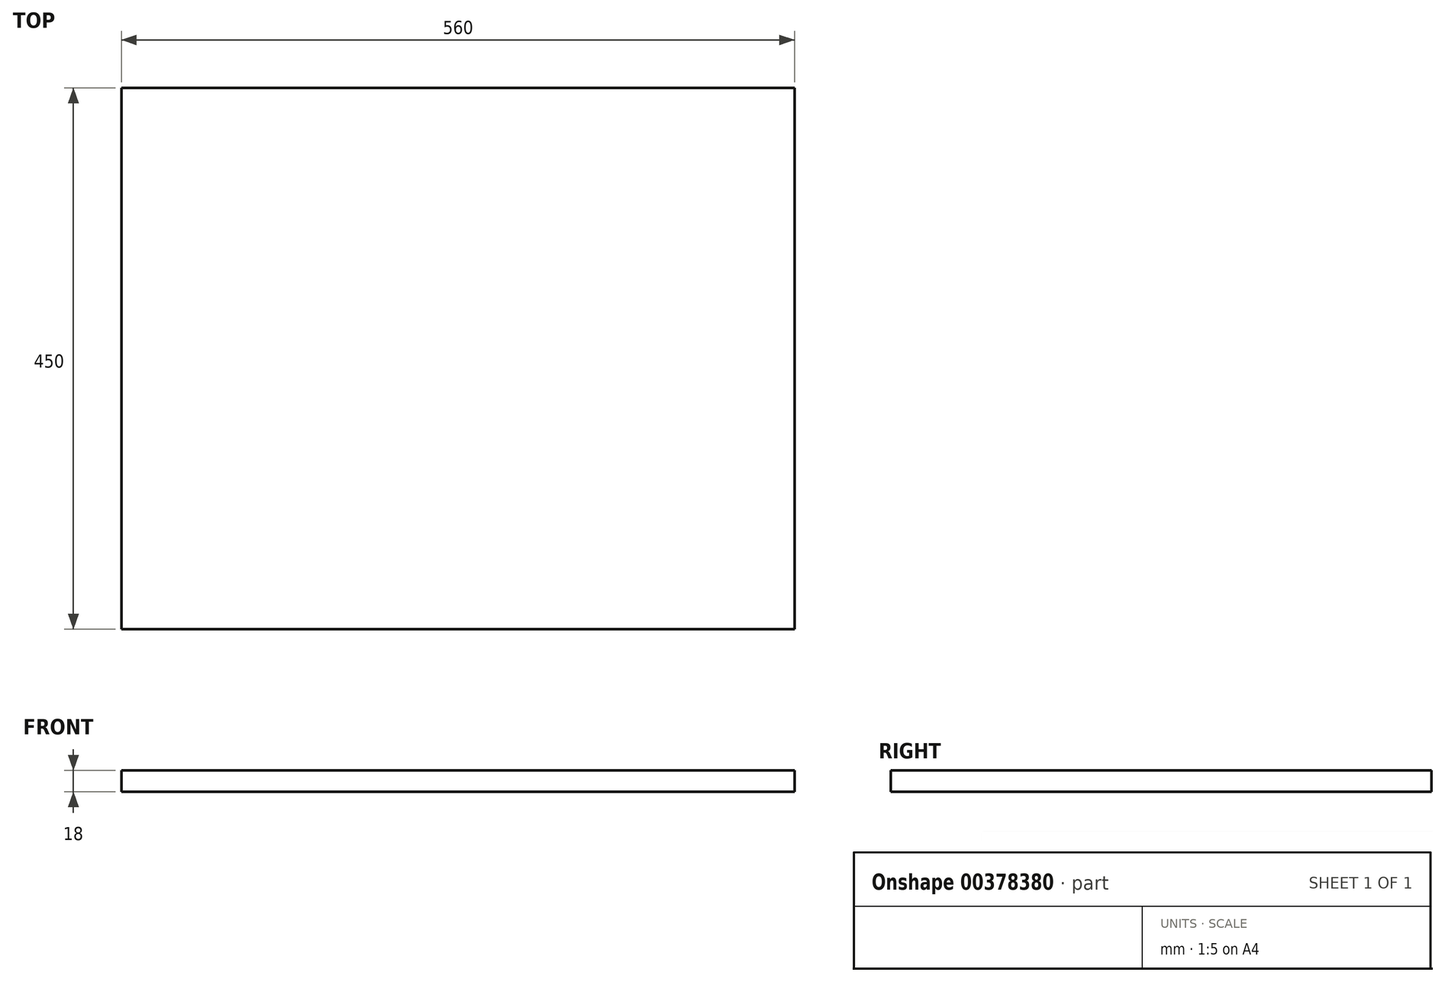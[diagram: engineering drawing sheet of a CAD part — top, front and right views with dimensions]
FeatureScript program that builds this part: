
annotation { "Feature Type Name" : "Feature", "Feature Type Description" : "" }
export const myFeature = defineFeature(function(context is Context, id is Id, definition is map)
    precondition{}
    {
        {
            var Q0;
            Q0=qCreatedBy(makeId("Top.planeOp"),FACE);
            var sketch = newSketch(context, id + "F0", { "sketchPlane" : qUnion([Q0])});
            skLineSegment(sketch, "E0.bottom", {"start": v(280, -225) * mm, "end": v(-280, -225) * mm});
            skLineSegment(sketch, "E0.top", {"start": v(280, 225) * mm, "end": v(-280, 225) * mm});
            skLineSegment(sketch, "E0.left", {"start": v(280, -225) * mm, "end": v(280, 225) * mm});
            skLineSegment(sketch, "E0.right", {"start": v(-280, -225) * mm, "end": v(-280, 225) * mm});
            skPoint(sketch, "E0.middle", {"position": v(0, 0) * mm});
            skSolve(sketch);
        }
        {
            var Q0;
            Q0 = qSketchRegion(id + "F0", true);
            extrude(context, id + "F1", {"entities" : qUnion([Q0]), "depth" : 18 * mm});
        }
    });
